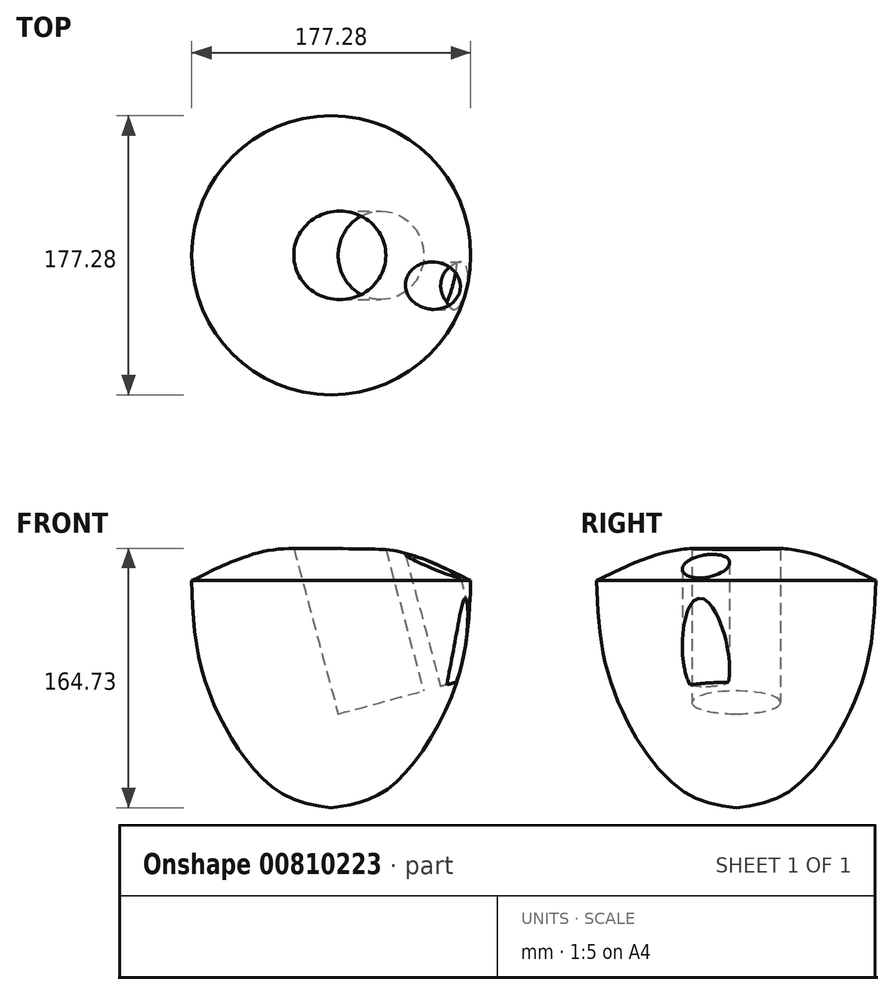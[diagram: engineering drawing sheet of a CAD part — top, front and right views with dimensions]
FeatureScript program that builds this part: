
annotation { "Feature Type Name" : "Feature", "Feature Type Description" : "" }
export const myFeature = defineFeature(function(context is Context, id is Id, definition is map)
    precondition{}
    {
        {
            var Q0;
            Q0=qCreatedBy(makeId("Front.planeOp"),FACE);
            var sketch = newSketch(context, id + "F0", { "sketchPlane" : qUnion([Q0])});
            skLineSegment(sketch, "E0", {"start": v(0, 84.68) * mm, "end": v(0, -78.77) * mm, "construction": true});
            skFitSpline(sketch, "E1", {"points": [v(0, -78.77) * mm, v(36.56, -66.35) * mm, v(79.42, 0) * mm, v(88.64, 65.45) * mm], "startDerivative": vector(137.19, 18.92) * mm, "endDerivative": vector(6.03, 180.87) * mm});
            skFitSpline(sketch, "E2", {"points": [v(88.64, 65.45) * mm, v(41.37, 84.28) * mm, v(0, 84.68) * mm], "startDerivative": vector(-90.6, 45) * mm, "endDerivative": vector(-86.62, -7.44) * mm});
            skLineSegment(sketch, "E3", {"start": v(0, 84.68) * mm, "end": v(0, -78.77) * mm});
            skSolve(sketch);
        }
        {
            var Q0;
            Q0 = qSketchRegion(id + "F0", true);
            var Q1;
            Q1=sQuery(id+"F0.wireOp",EDGE,"E3");
            revolve(context, id + "F1", {"surfaceOperationType" : NewSurfaceOperationType.NEW, "entities" : qUnion([Q0]), "axis" : qUnion([Q1]), "revolveType" : RevolveType.FULL});
        }
        {
            var Q0;
            Q0=qCreatedBy(makeId("Top.planeOp"),FACE);
            cPlane(context, id + "F2", {"entities" : qUnion([Q0]), "cplaneType" : CPlaneType.OFFSET, "offset" : 107 * mm, "width" : 150 * mm, "height" : 150 * mm});
        }
        {
            var Q0;
            Q0=qCreatedBy(id+"F2.planeOp",FACE);
            var sketch = newSketch(context, id + "F3", { "sketchPlane" : qUnion([Q0])});
            skLineSegment(sketch, "E4", {"start": v(0, 108.5) * mm, "end": v(0, -107.93) * mm});
            skSolve(sketch);
        }
        {
            var Q0;
            Q0=sQuery(id+"F3.wireOp",EDGE,"E4");
            cPlane(context, id + "F4", {"entities" : qUnion([Q0]), "cplaneType" : CPlaneType.LINE_ANGLE, "offset" : 25 * mm, "angle" : 15 * degree, "width" : 150 * mm, "height" : 150 * mm});
        }
        {
            var Q0;
            Q0=qCreatedBy(id+"F4.planeOp",FACE);
            var sketch = newSketch(context, id + "F5", { "sketchPlane" : qUnion([Q0])});
            skCircle(sketch, "E5", {"center": v(27.44, 0) * mm, "radius": 28.14 * mm});
            skCircle(sketch, "E6", {"center": v(81.78, 19.26) * mm, "radius": 15.05 * mm});
            skPoint(sketch, "E6.first.point", {"position": v(86.6, 5) * mm});
            skPoint(sketch, "E6.second.point", {"position": v(94.37, 27.51) * mm});
            skPoint(sketch, "E6.third.point", {"position": v(66.74, 18.98) * mm});
            skSolve(sketch);
        }
        {
            var Q0;
            Q0 = qSketchRegion(id + "F5", true);
            extrude(context, id + "F6", {"entities" : qUnion([Q0]), "operationType" : NewBodyOperationType.REMOVE, "oppositeDirection" : true, "depth" : 25 * mm, "offsetDistance" : 25 * mm, "hasSecondDirection" : true, "secondDirectionOppositeDirection" : false, "secondDirectionDepth" : 123 * mm});
        }
        {
            var Q0;
            Q0 = qSketchRegion(id + "F5", true);
            extrude(context, id + "F7", {"entities" : qUnion([Q0]), "operationType" : NewBodyOperationType.REMOVE, "oppositeDirection" : true, "depth" : 25 * mm, "offsetDistance" : 25 * mm});
        }
    });
